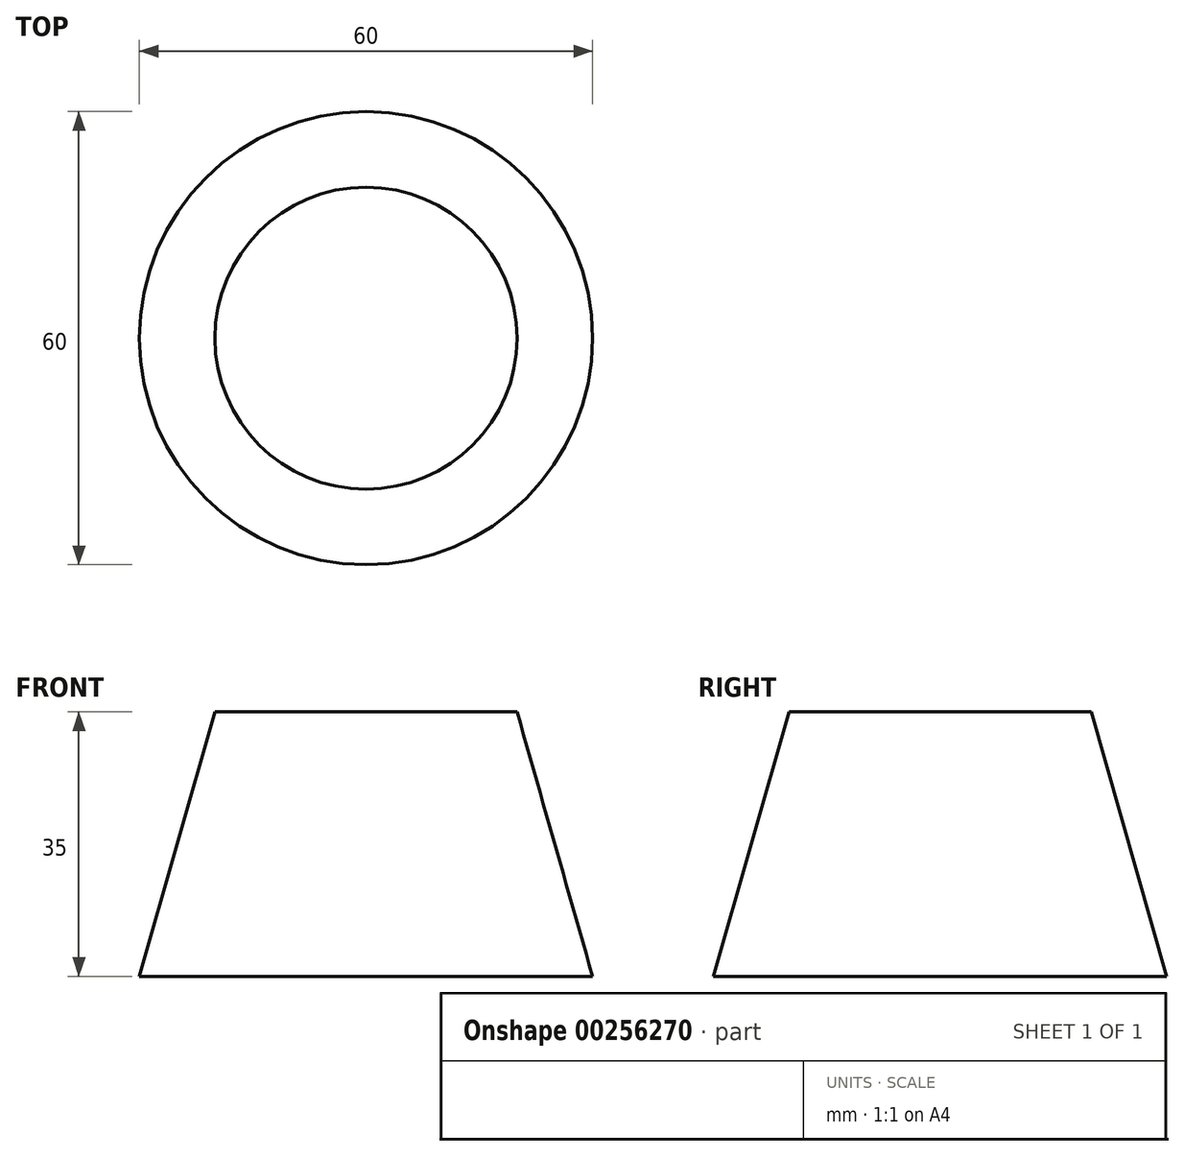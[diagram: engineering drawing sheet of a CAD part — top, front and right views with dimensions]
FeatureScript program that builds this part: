
annotation { "Feature Type Name" : "Feature", "Feature Type Description" : "" }
export const myFeature = defineFeature(function(context is Context, id is Id, definition is map)
    precondition{}
    {
        {
            var Q0;
            Q0=qCreatedBy(makeId("Front.planeOp"),FACE);
            var sketch = newSketch(context, id + "F0", { "sketchPlane" : qUnion([Q0])});
            skLineSegment(sketch, "E0", {"start": v(0, 0) * mm, "end": v(0, 35) * mm});
            skLineSegment(sketch, "E1", {"start": v(0, 35) * mm, "end": v(20, 35) * mm});
            skLineSegment(sketch, "E2", {"start": v(20, 35) * mm, "end": v(30, 0) * mm});
            skLineSegment(sketch, "E3", {"start": v(30, 0) * mm, "end": v(0, 0) * mm});
            skLineSegment(sketch, "E4", {"start": v(0, 63.26) * mm, "end": v(0, -51.78) * mm});
            skSolve(sketch);
        }
        {
            var Q0;
            {var subQ0=sQuery(id+"F0.wireOp",EDGE,"E1");Q0=makeQuery(id+"F0.imprint","IMPRINT",FACE,{"disambiguationData":[TD([[makeQuery(id+"F0.imprint","IMPRINT",EDGE,{"derivedFrom":subQ0}),-1.0]])]});}
            var Q1;
            Q1=sQuery(id+"F0.wireOp",EDGE,"E4");
            revolve(context, id + "F1", {"entities" : qUnion([Q0]), "axis" : qUnion([Q1]), "revolveType" : RevolveType.FULL});
        }
    });
